# Revit family: 00Wall Mounted Lavatory Faucet(long Spout)_TOTO_TLG07308
name_source: partatom
category: 衛生器具
revit_build: Autodesk Revit 2018 (Build: 20170223_1515(x64)
units: mm (PartAtom-declared; Revit-internal decimal feet)

## family parameters
OmniClass タイトル = Sanitary, Laundry, and Cleaning Equipment
OmniClass 番号 = 23.45.00.00
パーツ タイプ = 標準
ロード時にボイドで切り取り = いいえ
丸型コネクタ寸法 = 直径を使用
作業面ベース = いいえ
共有 = いいえ
常に垂直 = はい
部屋計算ポイント = いいえ

## types (1)
- 00Wall Mounted Lavatory Faucet(long Spout)_TOTO_TLG07308
    Finish = faucet_material
    Height = 110
    Length = 258.3  [stored 0.847441 ft]
    Width = 170
    タイプの説明 = without waste fitting/不含排水配件
    排気配管 = いいえ
    排水配管 = はい
    水配管 = はい
    温水配管 = はい
    製造元 = TOTO Ltd.
    説明 = Wall Mounted Lavatory Faucet(long Spout)/单柄双控暗装洗面器水嘴(长款)

note: [stored X ft] marks values corroborated as IEEE doubles in the binary element streams (Revit-internal decimal feet)

## geometry (parser evidence)
native form markers: Sweep x2
no freeform markers — native parametric forms only
